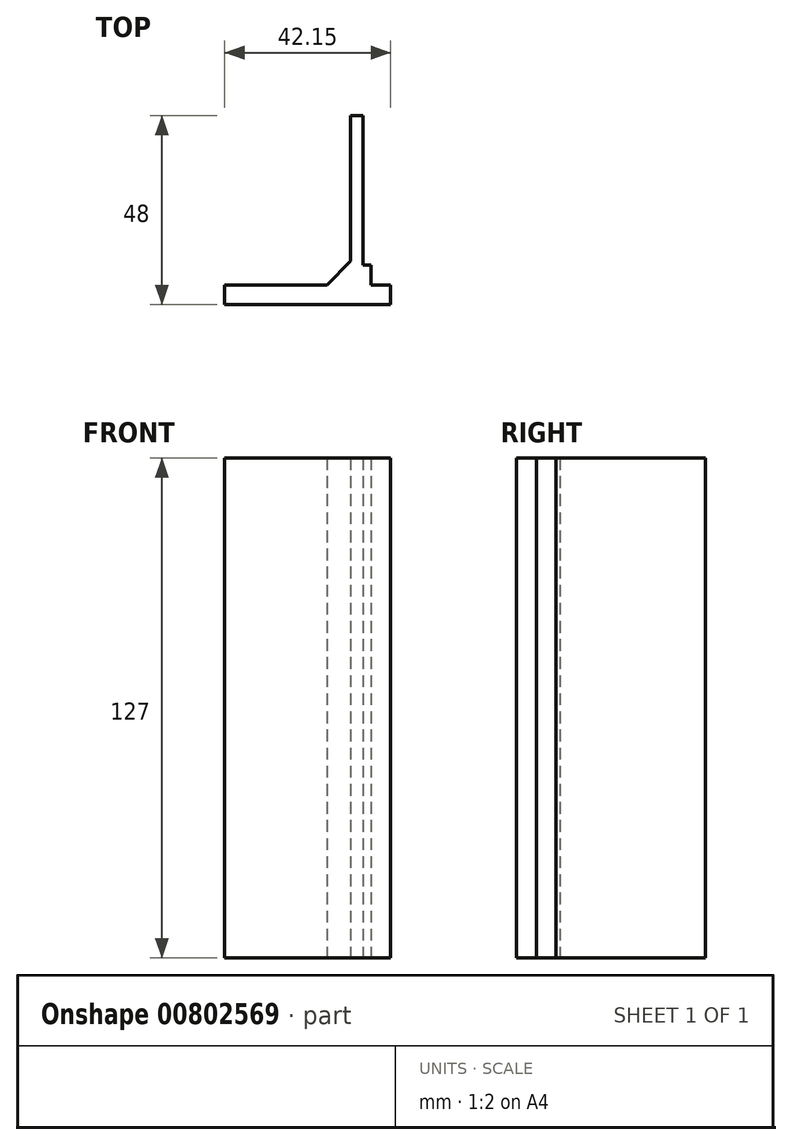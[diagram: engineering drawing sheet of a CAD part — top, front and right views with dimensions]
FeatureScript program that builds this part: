
annotation { "Feature Type Name" : "Feature", "Feature Type Description" : "" }
export const myFeature = defineFeature(function(context is Context, id is Id, definition is map)
    precondition{}
    {
        {
            var Q0;
            Q0=qCreatedBy(makeId("Top.planeOp"),FACE);
            var sketch = newSketch(context, id + "F0", { "sketchPlane" : qUnion([Q0])});
            skLineSegment(sketch, "E0.bottom", {"start": v(0, 0) * mm, "end": v(-32, 0) * mm});
            skLineSegment(sketch, "E0.top", {"start": v(0, -5) * mm, "end": v(-32, -5) * mm});
            skLineSegment(sketch, "E0.left", {"start": v(0, 0) * mm, "end": v(0, -5) * mm});
            skLineSegment(sketch, "E0.right", {"start": v(-32, 0) * mm, "end": v(-32, -5) * mm});
            skLineSegment(sketch, "E1.bottom", {"start": v(0, 0) * mm, "end": v(10.15, 0) * mm});
            skLineSegment(sketch, "E1.top", {"start": v(0, -5) * mm, "end": v(10.15, -5) * mm});
            skLineSegment(sketch, "E1.right", {"start": v(10.15, 0) * mm, "end": v(10.15, -5) * mm});
            skLineSegment(sketch, "E2.bottom", {"start": v(0, 0) * mm, "end": v(3.15, 0) * mm});
            skLineSegment(sketch, "E2.top", {"start": v(0, 43) * mm, "end": v(3.15, 43) * mm});
            skLineSegment(sketch, "E2.left", {"start": v(0, 0) * mm, "end": v(0, 43) * mm});
            skLineSegment(sketch, "E2.right", {"start": v(3.15, 0) * mm, "end": v(3.15, 43) * mm});
            skLineSegment(sketch, "E3.top", {"start": v(0, 6) * mm, "end": v(3.15, 6) * mm});
            skLineSegment(sketch, "E3.left", {"start": v(0, 0) * mm, "end": v(0, 6) * mm});
            skLineSegment(sketch, "E3.right", {"start": v(3.15, 0) * mm, "end": v(3.15, 6) * mm});
            skLineSegment(sketch, "E4.bottom", {"start": v(0, 0) * mm, "end": v(-6, 0) * mm});
            skLineSegment(sketch, "E4.top", {"start": v(0, -5) * mm, "end": v(-6, -5) * mm});
            skLineSegment(sketch, "E4.right", {"start": v(-6, 0) * mm, "end": v(-6, -5) * mm});
            skLineSegment(sketch, "E5.bottom", {"start": v(3.15, 0) * mm, "end": v(5.15, 0) * mm});
            skLineSegment(sketch, "E5.top", {"start": v(3.15, 5) * mm, "end": v(5.15, 5) * mm});
            skLineSegment(sketch, "E5.left", {"start": v(3.15, 0) * mm, "end": v(3.15, 5) * mm});
            skLineSegment(sketch, "E5.right", {"start": v(5.15, 0) * mm, "end": v(5.15, 5) * mm});
            skLineSegment(sketch, "E6", {"start": v(-6, 0) * mm, "end": v(0, 6) * mm});
            skSolve(sketch);
        }
        {
            var Q0;
            Q0 = qSketchRegion(id + "F0", true);
            extrude(context, id + "F1", {"entities" : qUnion([Q0]), "depth" : 127 * mm, "offsetDistance" : 25.4 * mm});
        }
    });
